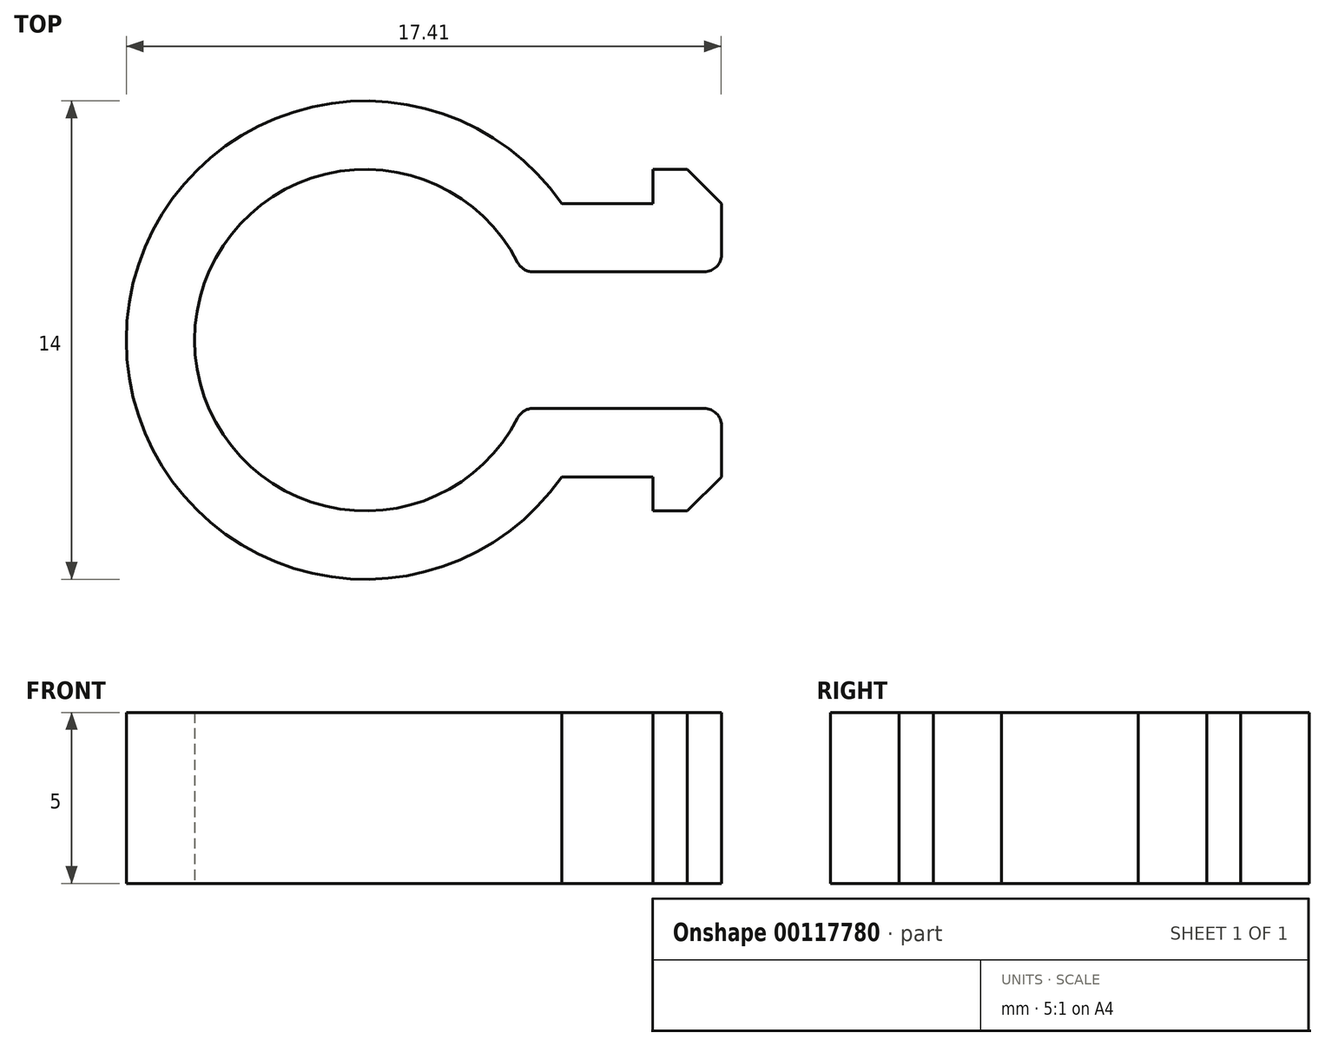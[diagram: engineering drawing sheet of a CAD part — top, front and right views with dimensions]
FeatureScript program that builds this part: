
annotation { "Feature Type Name" : "Feature", "Feature Type Description" : "" }
export const myFeature = defineFeature(function(context is Context, id is Id, definition is map)
    precondition{}
    {
        {
            var Q0;
            Q0=qCreatedBy(makeId("Top.planeOp"),FACE);
            var sketch = newSketch(context, id + "F0", { "sketchPlane" : qUnion([Q0])});
            skLineSegment(sketch, "E0", {"start": v(0, 0) * mm, "end": v(31.44, 0) * mm, "construction": true});
            skLineSegment(sketch, "E1.0", {"start": v(4.58, 2) * mm, "end": v(10.41, 2) * mm});
            skArc(sketch, "E2", {"start": v(4.58, 2) * mm, "mid": v(-5, 0) * mm, "end": v(4.58, -2) * mm});
            skLineSegment(sketch, "E3.0", {"start": v(4.58, -2) * mm, "end": v(10.41, -2) * mm});
            skArc(sketch, "E4.0", {"start": v(5.74, 4) * mm, "mid": v(-7, 0) * mm, "end": v(5.74, -4) * mm});
            skLineSegment(sketch, "E5.0", {"start": v(5.74, 4) * mm, "end": v(8.41, 4) * mm});
            skLineSegment(sketch, "E6.0", {"start": v(5.74, -4) * mm, "end": v(8.41, -4) * mm});
            skLineSegment(sketch, "E7.0", {"start": v(8.41, -5) * mm, "end": v(10.41, -5) * mm});
            skLineSegment(sketch, "E8.0", {"start": v(8.41, 5) * mm, "end": v(10.41, 5) * mm});
            skLineSegment(sketch, "E9", {"start": v(8.41, -5) * mm, "end": v(8.41, -4) * mm});
            skLineSegment(sketch, "E10.0", {"start": v(10.41, -5) * mm, "end": v(10.41, -2) * mm});
            skLineSegment(sketch, "E11.trimOffspring", {"start": v(8.41, 4) * mm, "end": v(8.41, 5) * mm});
            skLineSegment(sketch, "E12.trimOffspring", {"start": v(10.41, 2) * mm, "end": v(10.41, 5) * mm});
            skSolve(sketch);
        }
        {
            var Q0;
            Q0=makeQuery(id+"F0.imprint","IMPRINT",FACE,{"disambiguationData":[TD([[makeQuery(id+"F0.imprint","IMPRINT",EDGE,{"derivedFrom":sQuery(id+"F0.wireOp",EDGE,"E1.0")}),1.0]])]});
            extrude(context, id + "F1", {"entities" : qUnion([Q0]), "depth" : 5 * mm});
        }
        {
            var Q0;
            Q0=makeQuery(id+"F1.opExtrude","SWEPT_EDGE",EDGE,{"disambiguationData":[OSD([sQuery(id+"F0.wireOp",EDGE,"E1.0"),sQuery(id+"F0.wireOp",EDGE,"E12.trimOffspring")])]});
            var Q1;
            Q1=makeQuery(id+"F1.opExtrude","SWEPT_EDGE",EDGE,{"disambiguationData":[OSD([sQuery(id+"F0.wireOp",EDGE,"E1.0"),sQuery(id+"F0.wireOp",EDGE,"E2")])]});
            var Q2;
            Q2=makeQuery(id+"F1.opExtrude","SWEPT_EDGE",EDGE,{"disambiguationData":[OSD([sQuery(id+"F0.wireOp",EDGE,"E2"),sQuery(id+"F0.wireOp",EDGE,"E3.0")])]});
            var Q3;
            Q3=makeQuery(id+"F1.opExtrude","SWEPT_EDGE",EDGE,{"disambiguationData":[OSD([sQuery(id+"F0.wireOp",EDGE,"E3.0"),sQuery(id+"F0.wireOp",EDGE,"E10.0")])]});
            fillet(context, id + "F2", {"entities" : qUnion([Q0, Q1, Q2, Q3]), "radius" : .5 * mm, "tangentPropagation" : true, "allowEdgeOverflow" : false});
        }
        {
            var Q0;
            Q0=makeQuery(id+"F1.opExtrude","SWEPT_EDGE",EDGE,{"disambiguationData":[OSD([sQuery(id+"F0.wireOp",EDGE,"E7.0"),sQuery(id+"F0.wireOp",EDGE,"E10.0")])]});
            var Q1;
            Q1=makeQuery(id+"F1.opExtrude","SWEPT_EDGE",EDGE,{"disambiguationData":[OSD([sQuery(id+"F0.wireOp",EDGE,"E8.0"),sQuery(id+"F0.wireOp",EDGE,"E12.trimOffspring")])]});
            chamfer(context, id + "F3", {"entities" : qUnion([Q0, Q1]), "width" : 1 * mm, "tangentPropagation" : true});
        }
    });
